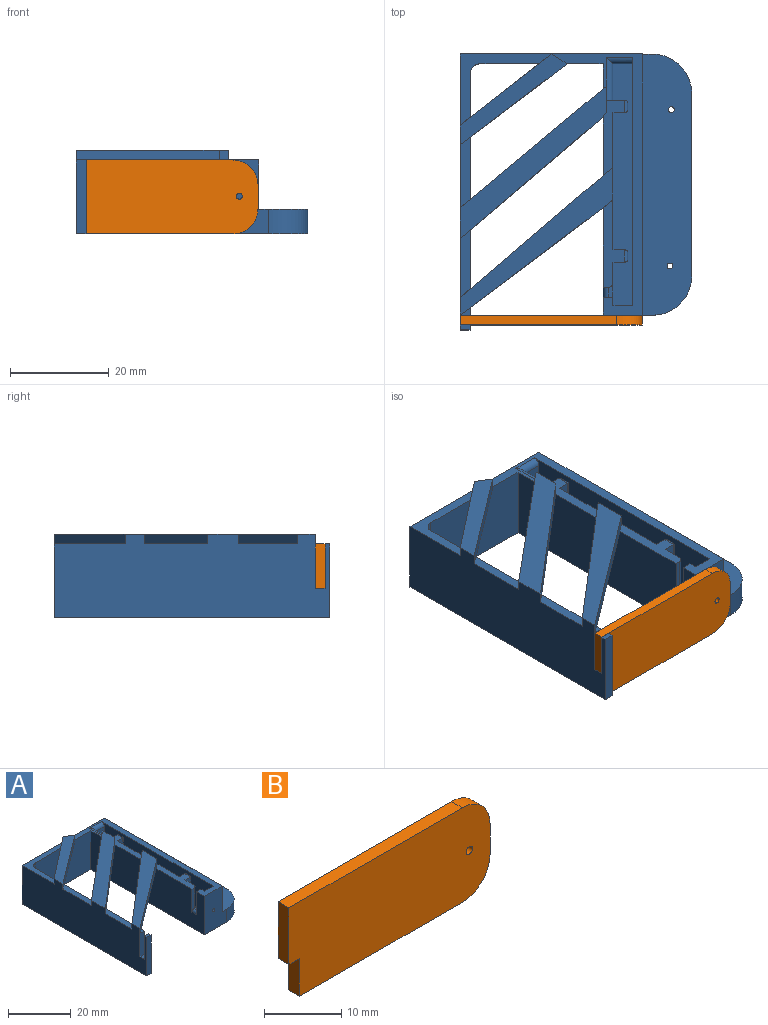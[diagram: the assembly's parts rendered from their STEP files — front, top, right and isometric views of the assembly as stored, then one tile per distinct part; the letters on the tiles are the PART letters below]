
ASSEMBLY  parts=2 mates=1
PART A: 79 faces, bbox 47x56x17 mm
  f0: plane 17.7x4.4mm, normal (0,0,1), area 39.7mm2, adj f8,f9,f23,f25,f38,f42,f45,f74
  f1: plane 2x1.5mm, normal (0,0,1), area 1.5mm2, adj f7,f58,f73
  f2: plane 15.32x4.4mm, normal (0,0,1), area 32.9mm2, adj f8,f9,f19,f21,f33,f67,f68,f75
  f3: plane 13.68x2mm, normal (0,0,1), area 23.9mm2, adj f7,f55,f66,f76
  f4: plane 53x18.5mm, normal (0,0,1), area 147.5mm2, adj f8,f9,f11,f12,f13,f16,f17,f40
  f5: plane 14.3x2mm, normal (0,0,1), area 25.4mm2, adj f7,f55,f61,f70
  f6: plane 2x1mm, normal (0,0,1), area 2mm2, adj f7,f55,f56,f57
  f7: plane 52x15mm, normal (1,0,0), area 757.8mm2, adj f1,f3,f5,f6,f10,f14,f56,f57
  f8: plane 51x15mm, normal (-1,0,0), area 743.3mm2, adj f0,f2,f4,f12,f14,f42,f43,f46
  f9: plane 49x15mm, normal (1,0,0), area 592mm2, adj f0,f2,f4,f15,f16,f18,f19,f21
  f10: plane 18.5x14.41mm, normal (0,0,1), area 58.5mm2, adj f7,f11,f54,f55,f60,f63
  f11: plane 39x15mm, normal (0,1,0), area 565mm2, adj f4,f10,f13,f14,f49,f51,f55
  f12: plane 15x10mm, normal (0,-1,0), area 128.9mm2, adj f4,f8,f13,f14,f47,f49,f50
  f13: plane 53x10mm, normal (1,0,0), area 530mm2, adj f4,f11,f12,f49
  f14: plane 56x47mm, normal (0,0,-1), area 1091.1mm2, adj f7,f8,f11,f12,f48,f50,f51,f52
  f15: plane 11.7x4mm, normal (0,-1,0), area 46.8mm2, adj f9,f17,f18,f40
  f16: plane 13x4mm, normal (0,1,0), area 50.9mm2, adj f4,f9,f17,f18,f47
  f17: plane 50.3x13mm, normal (-1,0,0), area 637.4mm2, adj f4,f15,f16,f18,f40
  f18: plane 49x4mm, normal (0,0,1), area 196mm2, adj f9,f15,f16,f17
  f19: plane 4.4x2.4mm, normal (0,-1,0), area 10.6mm2, adj f2,f9,f30,f34
  f20: plane 3.8x1.3mm, normal (1,0,0), area 4.9mm2, adj f29,f31,f33,f34
  f21: plane 4.4x3.7mm, normal (0,1,0), area 10.9mm2, adj f2,f9,f27,f31,f41
  f22: plane 2.4x1.3mm, normal (0,0,-1), area 3.1mm2, adj f9,f27,f29,f30
  f23: plane 4.4x2.4mm, normal (0,-1,0), area 10.6mm2, adj f0,f9,f35,f36
  f24: plane 4.4x1.3mm, normal (1,0,0), area 5.7mm2, adj f26,f36,f38,f39
  f25: plane 4.4x2.4mm, normal (0,1,0), area 10.6mm2, adj f0,f9,f37,f39
  f26: plane 3x1.3mm, normal (0,0,-1), area 3.9mm2, adj f9,f24,f35,f37
  f27: cylinder r=0.6mm len=2.4mm, axis (1,0,0), area 2.3mm2, adj f9,f21,f22,f28
  f28: sphere r=0.6mm, area 0.6mm2, adj f27,f29,f31
  f29: cylinder r=0.6mm len=1.3mm, axis (0,-1,0), area 1.2mm2, adj f20,f22,f28,f32
  f30: cylinder r=0.6mm len=2.4mm, axis (-1,0,0), area 2.3mm2, adj f9,f19,f22,f32
  f31: cylinder r=0.6mm len=4.4mm, axis (0,0,1), area 3.9mm2, adj f20,f21,f28,f33
  f32: sphere r=0.6mm, area 0.6mm2, adj f29,f30,f34
  f33: cylinder r=0.6mm len=2.5mm, axis (0,1,0), area 1.9mm2, adj f2,f20,f31,f34
  f34: cylinder r=0.6mm len=4.4mm, axis (0,0,-1), area 3.9mm2, adj f19,f20,f32,f33
  f35: cylinder r=0.6mm len=3mm, axis (-1,0,0), area 2.6mm2, adj f9,f23,f26,f36
  f36: cylinder r=0.6mm len=5mm, axis (0,0,-1), area 4.3mm2, adj f23,f24,f35,f38
  f37: cylinder r=0.6mm len=3mm, axis (1,0,0), area 2.6mm2, adj f9,f25,f26,f39
  f38: cylinder r=0.6mm len=2.5mm, axis (0,1,0), area 1.9mm2, adj f0,f24,f36,f39
  f39: cylinder r=0.6mm len=5mm, axis (0,0,1), area 4.3mm2, adj f24,f25,f37,f38
  f40: cylinder r=1.3mm len=5.3mm, axis (-1,0,0), area 9.1mm2, adj f4,f15,f17,f41
  f41: cylinder r=1.3mm len=8.66mm, axis (0,-1,0), area 16mm2, adj f4,f9,f21,f40,f68
  f42: plane 9x1mm, normal (0,-1,0), area 8.2mm2, adj f0,f8,f45,f46
  f43: plane 9x2mm, normal (0,1,0), area 16.2mm2, adj f4,f8,f9,f44,f46
  f44: plane 3x1mm, normal (0,0,1), area 2.2mm2, adj f9,f43,f45,f46
  f45: cylinder r=1mm len=8mm, axis (0,0,1), area 12.6mm2, adj f0,f9,f42,f44
  f46: cylinder r=1mm len=2mm, axis (0,1,0), area 3.1mm2, adj f8,f42,f43,f44
  f47: cylinder r=0.6mm len=2mm, axis (0,-1,0), area 7.5mm2, adj f12,f16
  f48: plane 37x5mm, normal (1,0,0), area 185mm2, adj f14,f49,f50,f51
  f49: plane 53x10mm, normal (0,0,1), area 500.3mm2, adj f11,f12,f13,f48,f50,f51,f52,f53
  f50: cylinder r=8mm len=8mm, axis (0,0,-1), area 62.8mm2, adj f12,f14,f48,f49
  f51: cylinder r=8mm len=8mm, axis (0,0,1), area 62.8mm2, adj f11,f14,f48,f49
  f52: cylinder r=0.6mm len=5mm, axis (0,0,1), area 18.8mm2, adj f14,f49
  f53: cylinder r=0.6mm len=5mm, axis (0,0,1), area 18.8mm2, adj f14,f49
  f54: plane 25x15mm, normal (0,-1,0), area 373.3mm2, adj f4,f8,f10,f14,f60,f61,f63,f65
  f55: plane 56x17mm, normal (-1,0,0), area 849.6mm2, adj f3,f5,f6,f10,f11,f14,f56,f57
  f56: plane 15x2mm, normal (0,-1,0), area 30mm2, adj f6,f7,f14,f55
  f57: plane 9x2mm, normal (0,1,0), area 18mm2, adj f6,f7,f55,f59
  f58: plane 9x2mm, normal (0,-1,0), area 18mm2, adj f1,f7,f55,f59
  f59: plane 2x2mm, normal (0,0,1), area 4mm2, adj f7,f55,f57,f58
  f60: cylinder r=2mm len=15mm, axis (0,0,1), area 47.1mm2, adj f7,f10,f14,f54
  f61: plane 21.71x16.4mm, normal (0.6,-0.8,0), area 61.8mm2, adj f5,f7,f54,f55,f62,f64,f65
  f62: plane 3.21x2mm, normal (0.53,0.85,0), area 7.6mm2, adj f4,f61,f63,f64
  f63: plane 18.5x14.41mm, normal (-0.61,0.79,0), area 52.2mm2, adj f7,f10,f54,f55,f62,f64,f65
  f64: plane 21.71x18.4mm, normal (0,0,1), area 85mm2, adj f55,f61,f62,f63
  f65: plane 19.71x14.89mm, normal (0,0,-1), area 71.2mm2, adj f7,f54,f61,f63
  f66: plane 29x24.68mm, normal (0.65,-0.76,0), area 86.8mm2, adj f3,f7,f8,f55,f67,f71,f72
  f67: plane 2x0.91mm, normal (0.79,-0.61,0), area 2.3mm2, adj f2,f66,f68,f71
  f68: plane 5.33x2mm, normal (1,0,0), area 10.7mm2, adj f2,f41,f67,f69,f71
  f69: plane 2x0.7mm, normal (-0.6,0.8,0), area 1.8mm2, adj f4,f68,f70,f71
  f70: plane 29x24.13mm, normal (-0.64,0.77,0), area 86mm2, adj f5,f7,f8,f55,f69,f71,f72
  f71: plane 30.92x29.7mm, normal (0,0,1), area 177.5mm2, adj f55,f66,f67,f68,f69,f70
  f72: plane 28.69x27mm, normal (0,0,-1), area 161.2mm2, adj f7,f8,f66,f70
  f73: plane 29x21.81mm, normal (0.6,-0.8,0), area 82.7mm2, adj f1,f7,f8,f55,f74,f77,f78
  f74: plane 2x2mm, normal (0.61,-0.8,0), area 5mm2, adj f0,f9,f73,f77
  f75: plane 2x2mm, normal (-0.64,0.77,0), area 5.2mm2, adj f2,f9,f76,f77
  f76: plane 29x24.74mm, normal (-0.65,0.76,0), area 86.9mm2, adj f3,f7,f8,f55,f75,f77,f78
  f77: plane 31x29.97mm, normal (0,0,1), area 159.3mm2, adj f9,f55,f73,f74,f75,f76
  f78: plane 27x26.81mm, normal (0,0,-1), area 138.8mm2, adj f7,f8,f73,f76
PART B: 11 faces, bbox 36.9x2x15 mm
  f0: plane 31.79x2mm, normal (0,0,1), area 63.6mm2, adj f1,f6,f7,f9
  f1: plane 9x2mm, normal (-1,0,0), area 18mm2, adj f0,f2,f6,f7
  f2: plane 2x1.94mm, normal (0,0,-1), area 3.9mm2, adj f1,f3,f6,f7
  f3: plane 6x2mm, normal (-1,0,0), area 12mm2, adj f2,f4,f6,f7
  f4: plane 29.85x2mm, normal (0,0,-1), area 59.7mm2, adj f3,f6,f7,f8
  f5: plane 4.84x2mm, normal (1,0,0), area 9.7mm2, adj f6,f7,f8,f9
  f6: plane 36.87x15mm, normal (0,-1,0), area 529.2mm2, adj f0,f1,f2,f3,f4,f5,f8,f9
  f7: plane 36.87x15mm, normal (0,1,0), area 529.2mm2, adj f0,f1,f2,f3,f4,f5,f8,f9
  f8: cylinder r=5.08mm len=5.08mm, axis (0,1,0), area 16mm2, adj f4,f5,f6,f7
  f9: cylinder r=5.08mm len=5.08mm, axis (0,-1,0), area 16mm2, adj f0,f5,f6,f7
  f10: cylinder r=0.6mm len=2mm, axis (0,1,0), area 7.5mm2, adj f6,f7
PLACE A at identity
PLACE B t=(-14.91,0,7.87)mm
MATE cylindrical B.f10 <-> A.f47  axis (0,1,0) through (4.13,0,7.61)mm
